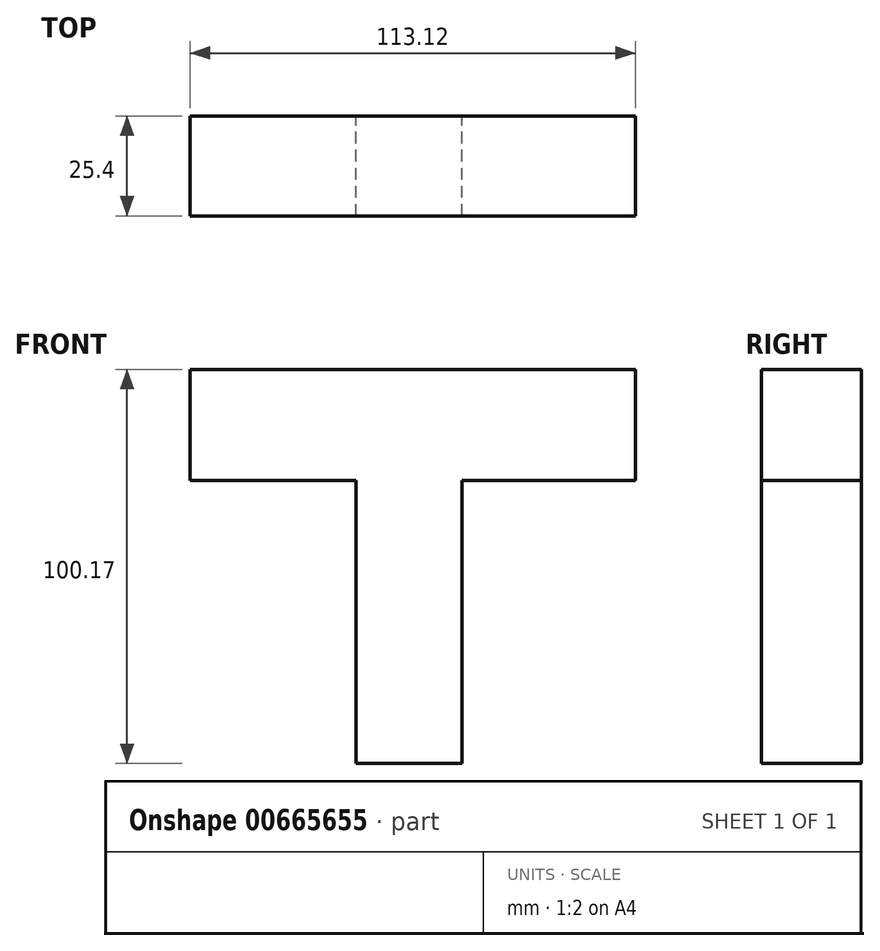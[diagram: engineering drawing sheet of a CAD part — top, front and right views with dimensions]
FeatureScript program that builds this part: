
annotation { "Feature Type Name" : "Feature", "Feature Type Description" : "" }
export const myFeature = defineFeature(function(context is Context, id is Id, definition is map)
    precondition{}
    {
        {
            var Q0;
            Q0=qCreatedBy(makeId("Front.planeOp"),FACE);
            var sketch = newSketch(context, id + "F0", { "sketchPlane" : qUnion([Q0])});
            skLineSegment(sketch, "E0", {"start": v(-15.94, 0) * mm, "end": v(-15.94, -55.02) * mm});
            skLineSegment(sketch, "E1", {"start": v(11, -2.57) * mm, "end": v(11, -55.02) * mm});
            skLineSegment(sketch, "E2", {"start": v(11, -2.57) * mm, "end": v(11, 0) * mm});
            skLineSegment(sketch, "E3", {"start": v(11, 0) * mm, "end": v(11, -55.02) * mm});
            skLineSegment(sketch, "E4", {"start": v(11, -55.02) * mm, "end": v(-15.94, -55.02) * mm});
            skLineSegment(sketch, "E5", {"start": v(-15.94, 0) * mm, "end": v(-15.94, 16.97) * mm});
            skLineSegment(sketch, "E6", {"start": v(11, 0) * mm, "end": v(11, 16.97) * mm});
            skLineSegment(sketch, "E7", {"start": v(11, 16.97) * mm, "end": v(55.02, 16.97) * mm});
            skLineSegment(sketch, "E8", {"start": v(55.02, 16.97) * mm, "end": v(55.02, 39.6) * mm});
            skLineSegment(sketch, "E9", {"start": v(55.02, 39.6) * mm, "end": v(55.02, 45.15) * mm});
            skLineSegment(sketch, "E10", {"start": v(55.02, 45.15) * mm, "end": v(-54.81, 45.15) * mm});
            skLineSegment(sketch, "E11", {"start": v(-17.8, 16.97) * mm, "end": v(-58.1, 16.97) * mm});
            skLineSegment(sketch, "E12", {"start": v(-58.1, 16.97) * mm, "end": v(-58.1, 45.15) * mm});
            skLineSegment(sketch, "E13", {"start": v(-58.1, 45.15) * mm, "end": v(-53.37, 45.15) * mm});
            skLineSegment(sketch, "E14", {"start": v(-15.94, 16.97) * mm, "end": v(-17.8, 16.97) * mm});
            skSolve(sketch);
        }
        {
            var Q0;
            Q0 = qSketchRegion(id + "F0", true);
            extrude(context, id + "F1", {"entities" : qUnion([Q0]), "depth" : 25.4 * mm, "offsetDistance" : 25.4 * mm});
        }
    });
